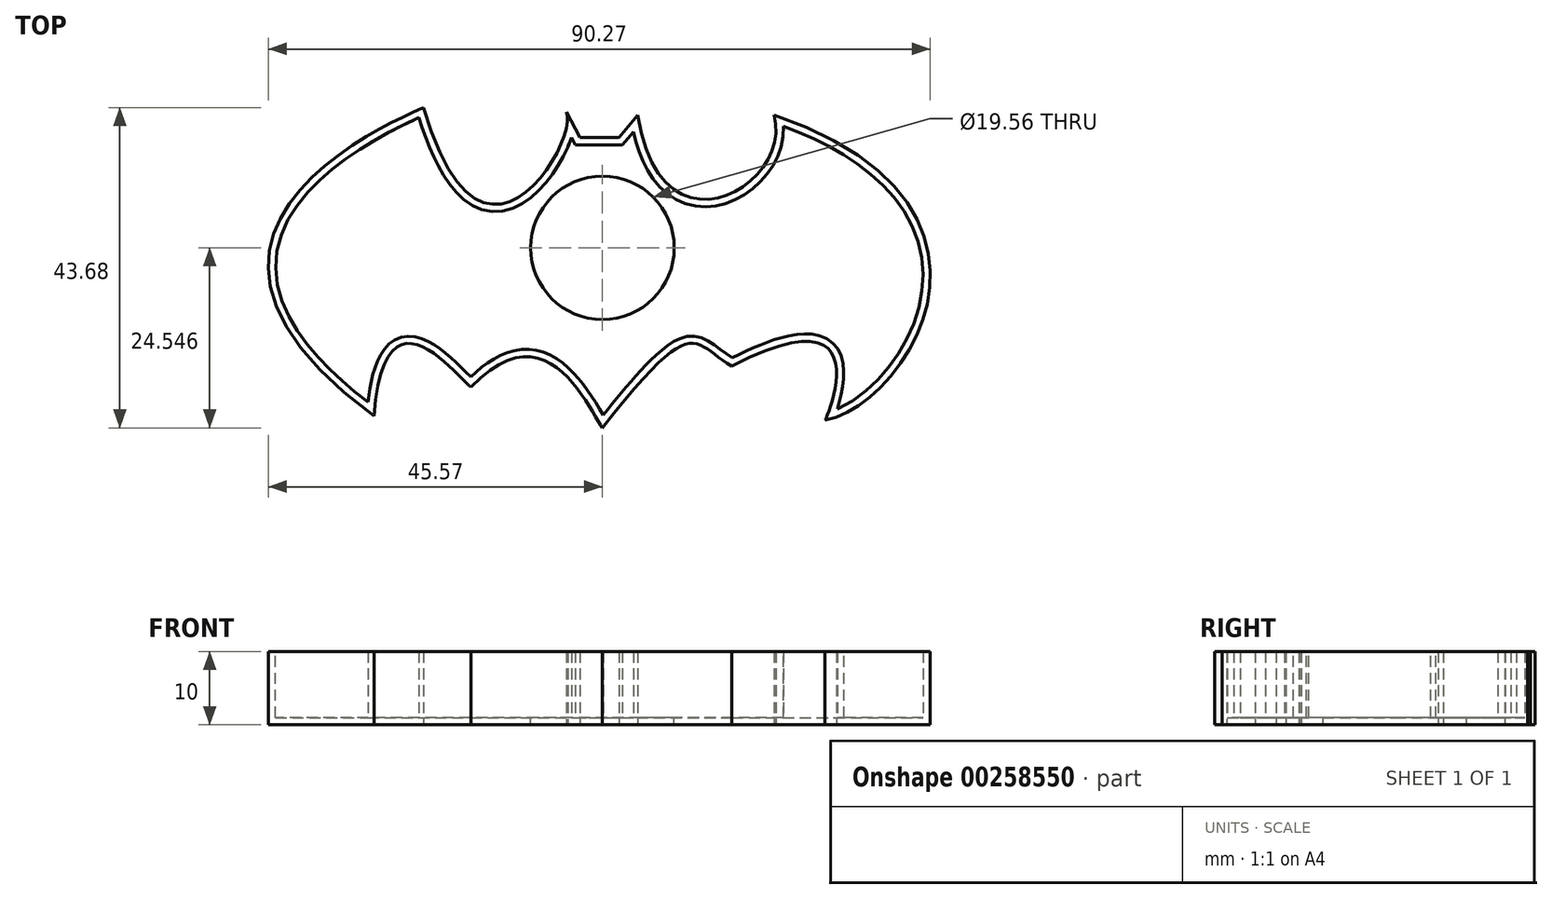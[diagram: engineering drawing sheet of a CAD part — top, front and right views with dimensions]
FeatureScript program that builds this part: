
annotation { "Feature Type Name" : "Feature", "Feature Type Description" : "" }
export const myFeature = defineFeature(function(context is Context, id is Id, definition is map)
    precondition{}
    {
        {
            var Q0;
            Q0=qCreatedBy(makeId("Top.planeOp"),FACE);
            var sketch = newSketch(context, id + "F0", { "sketchPlane" : qUnion([Q0])});
            skFitSpline(sketch, "E0", {"points": [v(-24.4, 21.33) * mm, v(-31.17, -20.71) * mm], "startDerivative": vector(-10.46, -4.92) * mm, "endDerivative": vector(103.36, -75.67) * mm});
            skFitSpline(sketch, "E1", {"points": [v(23.38, 20.3) * mm, v(30.35, -21.33) * mm], "startDerivative": vector(107.67, -36.91) * mm, "endDerivative": vector(-33.22, -6.15) * mm});
            skFitSpline(sketch, "E2", {"points": [v(23.38, 20.3) * mm, v(4.8, 20.3) * mm], "startDerivative": vector(8.38, -28.3) * mm, "endDerivative": vector(-9.35, 60.9) * mm});
            skFitSpline(sketch, "E3", {"points": [v(-4.92, 20.71) * mm, v(-24.4, 21.33) * mm], "startDerivative": vector(5.54, -10.46) * mm, "endDerivative": vector(-24, 82.44) * mm});
            skLineSegment(sketch, "E4", {"start": v(-4.92, 20.71) * mm, "end": v(-3.08, 17.23) * mm});
            skLineSegment(sketch, "E5", {"start": v(2.26, 17.23) * mm, "end": v(4.8, 20.3) * mm});
            skLineSegment(sketch, "E6", {"start": v(-3.08, 17.23) * mm, "end": v(2.26, 17.23) * mm});
            skFitSpline(sketch, "E7", {"points": [v(-31.17, -20.71) * mm, v(-17.94, -16.82) * mm], "startDerivative": vector(4.3, 55.37) * mm, "endDerivative": vector(6.77, -5.54) * mm});
            skFitSpline(sketch, "E8", {"points": [v(-17.94, -16.82) * mm, v(0, -22.35) * mm], "startDerivative": vector(30.97, 32.9) * mm, "endDerivative": vector(6.03, -8.27) * mm});
            skFitSpline(sketch, "E9", {"points": [v(0, -22.35) * mm, v(17.64, -13.95) * mm], "startDerivative": vector(38.14, 48.86) * mm, "endDerivative": vector(16, -9.23) * mm});
            skFitSpline(sketch, "E10", {"points": [v(17.64, -13.95) * mm, v(30.35, -21.33) * mm], "startDerivative": vector(59.06, 30.76) * mm, "endDerivative": vector(-2.46, -4.92) * mm});
            skSolve(sketch);
        }
        {
            var Q0;
            Q0=makeQuery(id+"F0.imprint","IMPRINT",FACE,{"disambiguationData":[TD([[makeQuery(id+"F0.imprint","IMPRINT",EDGE,{"derivedFrom":sQuery(id+"F0.wireOp",EDGE,"E0")}),1.0]])]});
            extrude(context, id + "F1", {"entities" : qUnion([Q0]), "depth" : 10 * mm});
        }
        {
            var Q0;
            Q0=makeQuery(id+"F1.opExtrude","CAP_FACE",FACE,{"disambiguationData":[OSD([sQuery(id+"F0.wireOp",EDGE,"E0"),sQuery(id+"F0.wireOp",EDGE,"E1"),sQuery(id+"F0.wireOp",EDGE,"E2"),sQuery(id+"F0.wireOp",EDGE,"E3"),sQuery(id+"F0.wireOp",EDGE,"E4"),sQuery(id+"F0.wireOp",EDGE,"E5"),sQuery(id+"F0.wireOp",EDGE,"E6"),sQuery(id+"F0.wireOp",EDGE,"E7"),sQuery(id+"F0.wireOp",EDGE,"E8"),sQuery(id+"F0.wireOp",EDGE,"E9"),sQuery(id+"F0.wireOp",EDGE,"E10")])],"isStart":false});
            shell(context, id + "F2", {"entities" : qUnion([Q0]), "thickness" : 1 * mm});
        }
        {
            var Q0;
            Q0=makeQuery(id+"F2.opShell","OFFSET_FACE",FACE,{"disambiguationData":[OSD([sQuery(id+"F0.wireOp",EDGE,"E0"),sQuery(id+"F0.wireOp",EDGE,"E1"),sQuery(id+"F0.wireOp",EDGE,"E2"),sQuery(id+"F0.wireOp",EDGE,"E3"),sQuery(id+"F0.wireOp",EDGE,"E4"),sQuery(id+"F0.wireOp",EDGE,"E5"),sQuery(id+"F0.wireOp",EDGE,"E6"),sQuery(id+"F0.wireOp",EDGE,"E7"),sQuery(id+"F0.wireOp",EDGE,"E8"),sQuery(id+"F0.wireOp",EDGE,"E9"),sQuery(id+"F0.wireOp",EDGE,"E10")])]});
            var sketch = newSketch(context, id + "F3", { "sketchPlane" : qUnion([Q0])});
            skCircle(sketch, "E11", {"center": v(0, 2.2) * mm, "radius": 9.78 * mm});
            skSolve(sketch);
        }
        {
            var Q0;
            Q0 = qSketchRegion(id + "F3", true);
            extrude(context, id + "F4", {"entities" : qUnion([Q0]), "operationType" : NewBodyOperationType.REMOVE, "oppositeDirection" : true, "depth" : 25 * mm});
        }
    });
